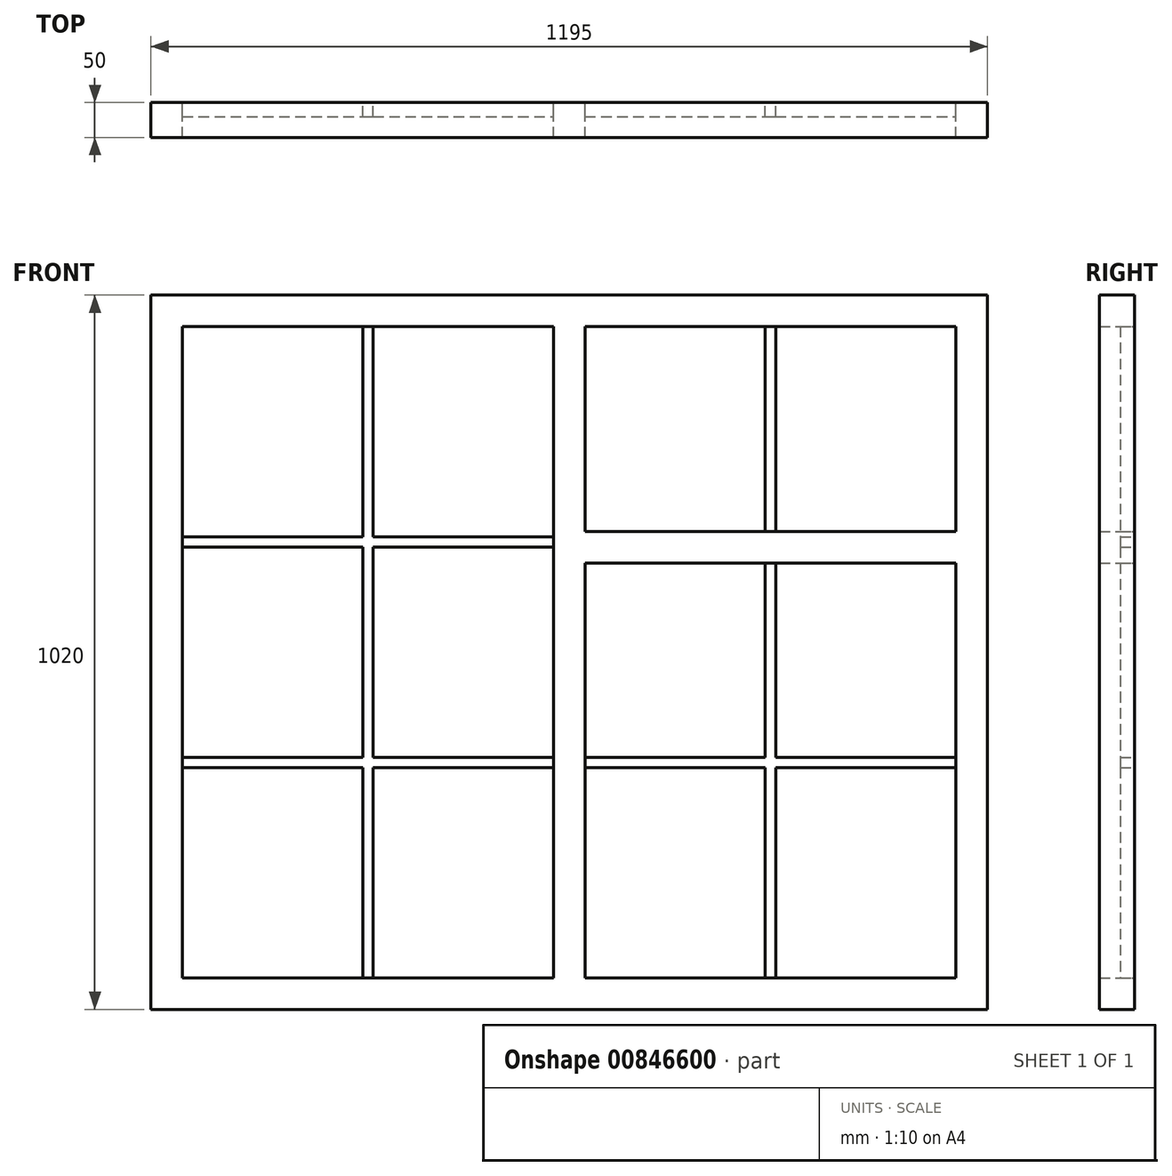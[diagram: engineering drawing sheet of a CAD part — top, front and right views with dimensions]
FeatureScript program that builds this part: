
annotation { "Feature Type Name" : "Feature", "Feature Type Description" : "" }
export const myFeature = defineFeature(function(context is Context, id is Id, definition is map)
    precondition{}
    {
        {
            var Q0;
            Q0=qCreatedBy(makeId("Front.planeOp"),FACE);
            var sketch = newSketch(context, id + "F0", { "sketchPlane" : qUnion([Q0])});
            skLineSegment(sketch, "E0.bottom", {"start": v(0, 0) * mm, "end": v(1195, 0) * mm});
            skLineSegment(sketch, "E0.top", {"start": v(0, 1020) * mm, "end": v(1195, 1020) * mm});
            skLineSegment(sketch, "E0.left", {"start": v(0, 0) * mm, "end": v(0, 1020) * mm});
            skLineSegment(sketch, "E0.right", {"start": v(1195, 0) * mm, "end": v(1195, 1020) * mm});
            skLineSegment(sketch, "E1.bottom", {"start": v(45, 975) * mm, "end": v(575, 975) * mm});
            skLineSegment(sketch, "E1.top", {"start": v(45, 45) * mm, "end": v(575, 45) * mm});
            skLineSegment(sketch, "E1.left", {"start": v(45, 975) * mm, "end": v(45, 45) * mm});
            skLineSegment(sketch, "E1.right", {"start": v(575, 975) * mm, "end": v(575, 45) * mm});
            skLineSegment(sketch, "E2.bottom", {"start": v(620, 975) * mm, "end": v(1150, 975) * mm});
            skLineSegment(sketch, "E2.top", {"start": v(620, 682.5) * mm, "end": v(1150, 682.5) * mm});
            skLineSegment(sketch, "E2.left", {"start": v(620, 975) * mm, "end": v(620, 682.5) * mm});
            skLineSegment(sketch, "E2.right", {"start": v(1150, 975) * mm, "end": v(1150, 682.5) * mm});
            skLineSegment(sketch, "E3.bottom", {"start": v(620, 637.5) * mm, "end": v(1150, 637.5) * mm});
            skLineSegment(sketch, "E3.top", {"start": v(620, 45) * mm, "end": v(1150, 45) * mm});
            skLineSegment(sketch, "E3.left", {"start": v(620, 637.5) * mm, "end": v(620, 45) * mm});
            skLineSegment(sketch, "E3.right", {"start": v(1150, 637.5) * mm, "end": v(1150, 45) * mm});
            skSolve(sketch);
        }
        {
            var Q0;
            Q0=qSketchRegion(id+"F0",true);
            extrude(context, id + "F1", {"entities" : qUnion([Q0]), "depth" : 50 * mm, "offsetDistance" : 25 * mm});
        }
        {
            var Q0;
            Q0=qCreatedBy(makeId("Front.planeOp"),FACE);
            var sketch = newSketch(context, id + "F2", { "sketchPlane" : qUnion([Q0])});
            skLineSegment(sketch, "E4.bottom", {"start": v(302.5, 975) * mm, "end": v(317.5, 975) * mm});
            skLineSegment(sketch, "E4.top", {"start": v(302.5, 45) * mm, "end": v(317.5, 45) * mm});
            skLineSegment(sketch, "E4.left", {"start": v(302.5, 975) * mm, "end": v(302.5, 675) * mm});
            skLineSegment(sketch, "E4.right", {"start": v(317.5, 975) * mm, "end": v(317.5, 675) * mm});
            skLineSegment(sketch, "E5.bottom", {"start": v(45, 675) * mm, "end": v(302.5, 675) * mm});
            skLineSegment(sketch, "E5.top", {"start": v(45, 660) * mm, "end": v(302.5, 660) * mm});
            skLineSegment(sketch, "E5.left", {"start": v(45, 675) * mm, "end": v(45, 660) * mm});
            skLineSegment(sketch, "E5.right", {"start": v(575, 675) * mm, "end": v(575, 660) * mm});
            skLineSegment(sketch, "E6.bottom", {"start": v(45, 360) * mm, "end": v(302.5, 360) * mm});
            skLineSegment(sketch, "E6.top", {"start": v(45, 345) * mm, "end": v(302.5, 345) * mm});
            skLineSegment(sketch, "E6.left", {"start": v(45, 360) * mm, "end": v(45, 345) * mm});
            skLineSegment(sketch, "E6.right", {"start": v(575, 360) * mm, "end": v(575, 345) * mm});
            skLineSegment(sketch, "E7.trimOffspring", {"start": v(317.5, 675) * mm, "end": v(575, 675) * mm});
            skLineSegment(sketch, "E8.trimOffspring", {"start": v(302.5, 660) * mm, "end": v(302.5, 360) * mm});
            skLineSegment(sketch, "E9.trimOffspring", {"start": v(317.5, 660) * mm, "end": v(575, 660) * mm});
            skLineSegment(sketch, "E10.trimOffspring", {"start": v(317.5, 660) * mm, "end": v(317.5, 360) * mm});
            skLineSegment(sketch, "E11.trimOffspring", {"start": v(317.5, 360) * mm, "end": v(575, 360) * mm});
            skLineSegment(sketch, "E12.trimOffspring", {"start": v(302.5, 345) * mm, "end": v(302.5, 45) * mm});
            skLineSegment(sketch, "E13.trimOffspring", {"start": v(317.5, 345) * mm, "end": v(575, 345) * mm});
            skLineSegment(sketch, "E14.trimOffspring", {"start": v(317.5, 345) * mm, "end": v(317.5, 45) * mm});
            skLineSegment(sketch, "E15.bottom", {"start": v(620, 360) * mm, "end": v(877.5, 360) * mm});
            skLineSegment(sketch, "E15.top", {"start": v(620, 345) * mm, "end": v(877.5, 345) * mm});
            skLineSegment(sketch, "E15.left", {"start": v(620, 360) * mm, "end": v(620, 345) * mm});
            skLineSegment(sketch, "E15.right", {"start": v(1150, 360) * mm, "end": v(1150, 345) * mm});
            skLineSegment(sketch, "E16.bottom", {"start": v(877.5, 637.5) * mm, "end": v(892.5, 637.5) * mm});
            skLineSegment(sketch, "E16.top", {"start": v(877.5, 45) * mm, "end": v(892.5, 45) * mm});
            skLineSegment(sketch, "E16.left", {"start": v(877.5, 637.5) * mm, "end": v(877.5, 360) * mm});
            skLineSegment(sketch, "E16.right", {"start": v(892.5, 637.5) * mm, "end": v(892.5, 360) * mm});
            skLineSegment(sketch, "E17.bottom", {"start": v(877.5, 975) * mm, "end": v(892.5, 975) * mm});
            skLineSegment(sketch, "E17.top", {"start": v(877.5, 682.5) * mm, "end": v(892.5, 682.5) * mm});
            skLineSegment(sketch, "E17.left", {"start": v(877.5, 975) * mm, "end": v(877.5, 682.5) * mm});
            skLineSegment(sketch, "E17.right", {"start": v(892.5, 975) * mm, "end": v(892.5, 682.5) * mm});
            skLineSegment(sketch, "E18.trimOffspring", {"start": v(892.5, 360) * mm, "end": v(1150, 360) * mm});
            skLineSegment(sketch, "E19.trimOffspring", {"start": v(877.5, 345) * mm, "end": v(877.5, 45) * mm});
            skLineSegment(sketch, "E20.trimOffspring", {"start": v(892.5, 345) * mm, "end": v(1150, 345) * mm});
            skLineSegment(sketch, "E21.trimOffspring", {"start": v(892.5, 345) * mm, "end": v(892.5, 45) * mm});
            skSolve(sketch);
        }
        {
            var Q0;
            Q0=qSketchRegion(id+"F2",true);
            extrude(context, id + "F3", {"entities" : qUnion([Q0]), "operationType" : NewBodyOperationType.ADD, "depth" : 20 * mm, "offsetDistance" : 25 * mm});
        }
    });
